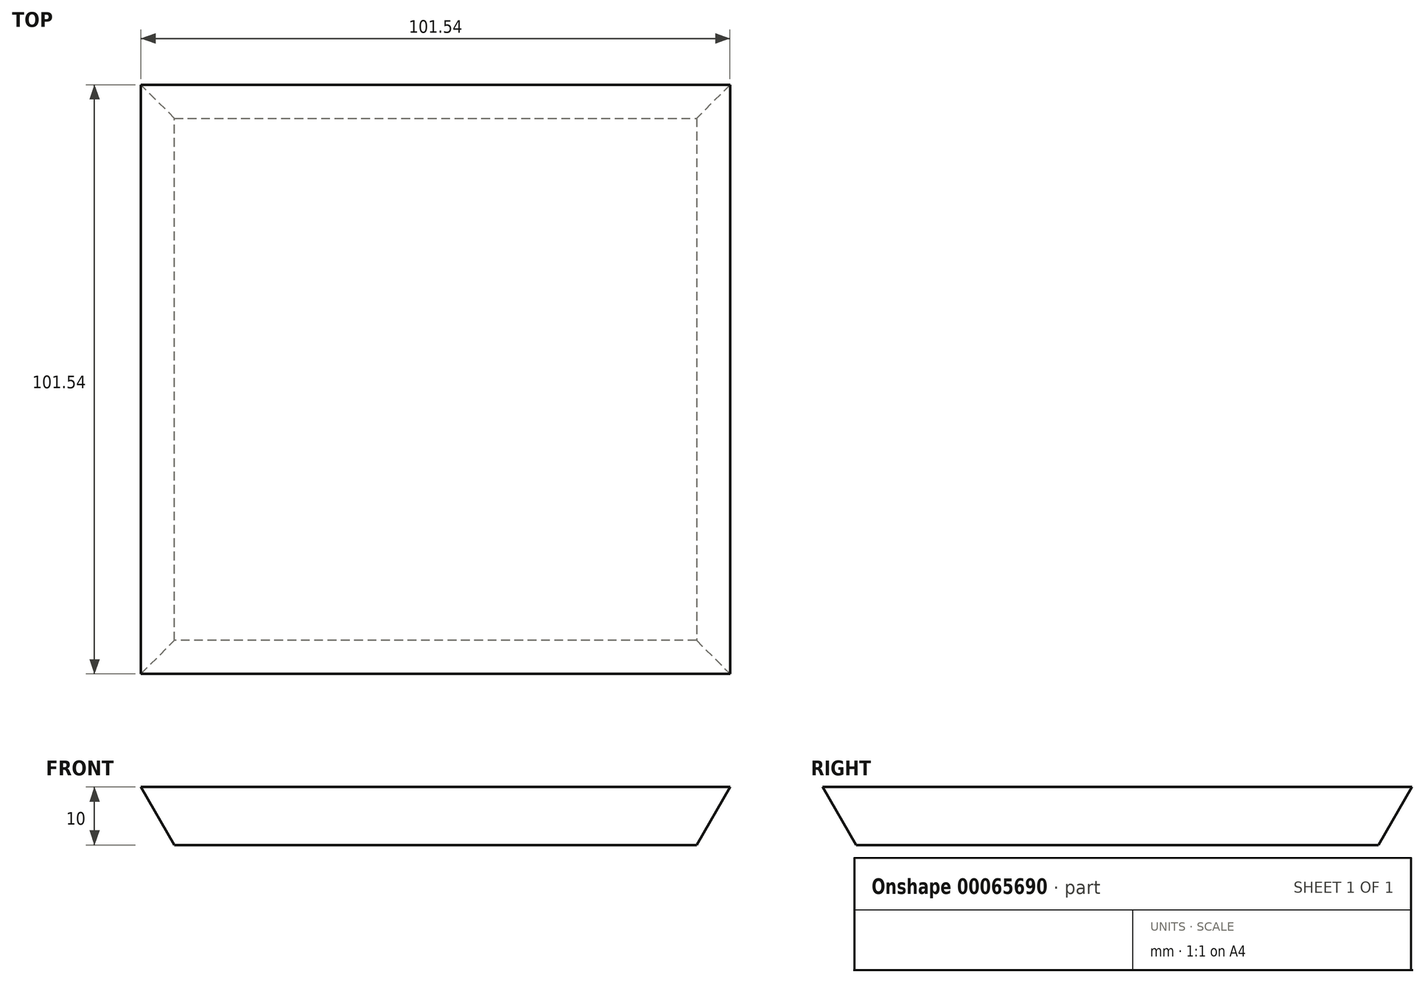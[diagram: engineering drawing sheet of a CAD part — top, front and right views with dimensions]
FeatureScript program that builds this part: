
annotation { "Feature Type Name" : "Feature", "Feature Type Description" : "" }
export const myFeature = defineFeature(function(context is Context, id is Id, definition is map)
    precondition{}
    {
        {
            assignVariable(context, id + "F0", {"name" : "h", "anyValue" : 10});
        }
        {
            var Q0;
            Q0=qCreatedBy(makeId("Top.planeOp"),FACE);
            var sketch = newSketch(context, id + "F1", { "sketchPlane" : qUnion([Q0])});
            skLineSegment(sketch, "E0.bottom", {"start": v(-45, 45) * mm, "end": v(45, 45) * mm});
            skLineSegment(sketch, "E0.top", {"start": v(-45, -45) * mm, "end": v(45, -45) * mm});
            skLineSegment(sketch, "E0.left", {"start": v(-45, 45) * mm, "end": v(-45, -45) * mm});
            skLineSegment(sketch, "E0.right", {"start": v(45, 45) * mm, "end": v(45, -45) * mm});
            skLineSegment(sketch, "E1", {"start": v(0, 0) * mm, "end": v(0, 45) * mm, "construction": true});
            skLineSegment(sketch, "E2", {"start": v(0, 0) * mm, "end": v(45, 0) * mm, "construction": true});
            skSolve(sketch);
        }
        {
            var Q0;
            Q0=makeQuery(id+"F1.imprint","IMPRINT",FACE,{"disambiguationData":[TD([[makeQuery(id+"F1.imprint","IMPRINT",EDGE,{"derivedFrom":sQuery(id+"F1.wireOp",EDGE,"E0.bottom")}),-1.0]])]});
            extrude(context, id + "F2", {"entities" : qUnion([Q0]), "depth" : (getVariable(context, 'h')) * mm, "hasDraft" : true, "draftAngle" : 30 * degree});
        }
    });
